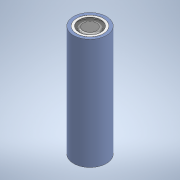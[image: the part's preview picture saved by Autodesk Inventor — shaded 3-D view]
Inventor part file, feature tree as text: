
AUTODESK INVENTOR PART (.ipt)
format: ipt  version: 2022 (Build 260153000, 153)  size: 149,504 bytes
history: native  units: mm
features: extrude x6, sketch x6, fillet x1
ambient origin geometry x8: Origin, YZ Plane, XZ Plane, XY Plane, X Axis, Y Axis, Z Axis, Center Point
bodies: Solid1 (feature_tree)
feature tree (13):
  extrude  "Extrusion1"  Depth=70.8mm TaperAngle=0.0deg
  extrude  "Extrusion2"  Depth=2.0mm TaperAngle=0.0deg
  extrude  "Extrusion3"  Depth=1.75mm TaperAngle=0.0deg
  extrude  "Extrusion4"  Depth=1.5mm TaperAngle=0.0deg
  fillet  "Fillet1"  Radius=1.5mm
  extrude  "Extrusion5"  Depth=0.05mm TaperAngle=0.0deg
  extrude  "Extrusion6"  [1 undecoded]
  sketch  "Sketch1"  dims[d0=21.0mm d1=70.8mm d2=0.0mm]
  sketch  "Sketch2"  dims[d3=3.5mm d4=2.0mm d5=0.0mm]
  sketch  "Sketch3"  dims[d6=2.0mm d7=1.75mm d8=0.0mm]
  sketch  "Sketch4"  dims[d9=11.5mm d10=1.5mm d11=0.0mm d12=1.5mm]
  sketch  "Sketch5"  dims[d13=0.05mm d14=0.0mm d15=0.05mm d16=0.0mm]
  sketch  "Sketch6"
note: 1 required parameter value undecoded (feature->parameter linkage not recoverable at this tier; creation-order binding heuristic only, values carry confidence <= 0.55)
